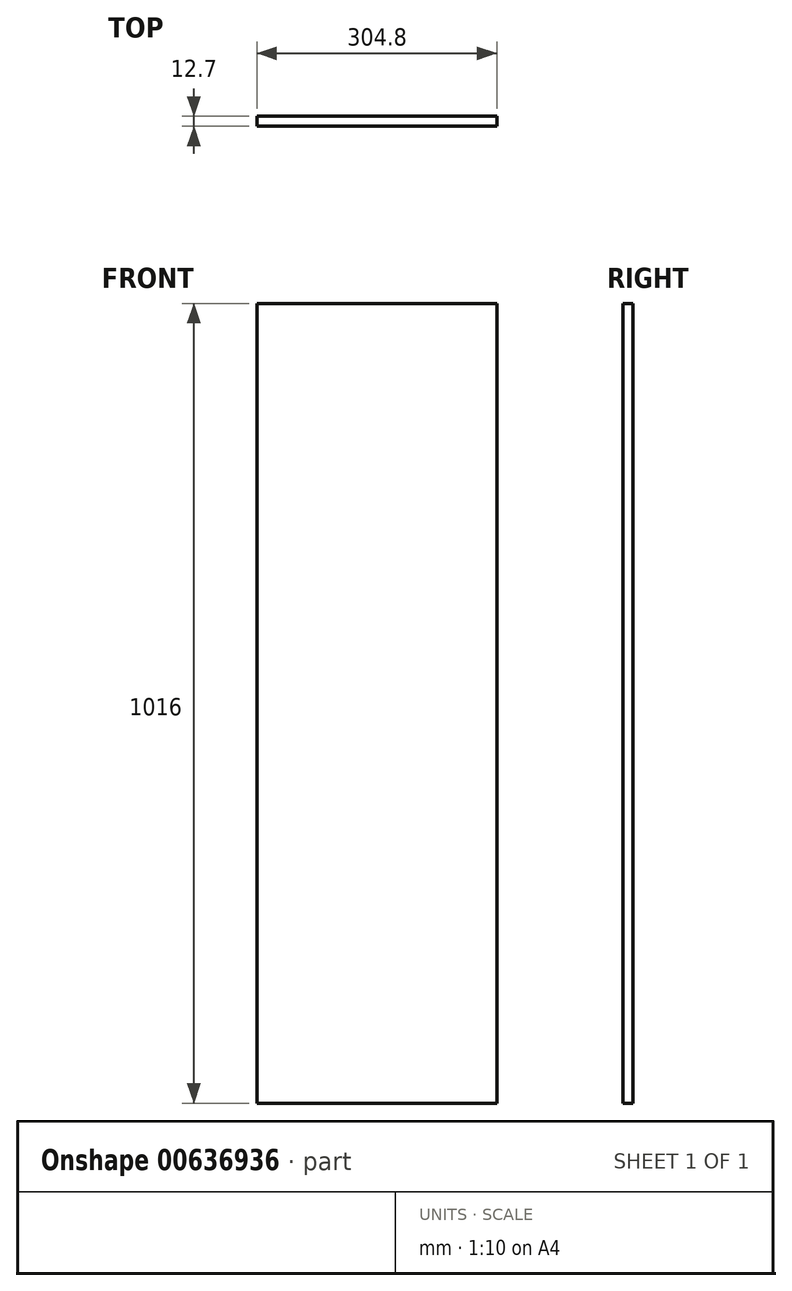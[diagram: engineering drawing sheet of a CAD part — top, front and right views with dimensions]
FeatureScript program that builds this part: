
annotation { "Feature Type Name" : "Feature", "Feature Type Description" : "" }
export const myFeature = defineFeature(function(context is Context, id is Id, definition is map)
    precondition{}
    {
        {
            var Q0;
            Q0=qCreatedBy(makeId("Front.planeOp"),FACE);
            var sketch = newSketch(context, id + "F0", { "sketchPlane" : qUnion([Q0])});
            skLineSegment(sketch, "E0.bottom", {"start": v(0, 0) * mm, "end": v(304.8, 0) * mm});
            skLineSegment(sketch, "E0.top", {"start": v(0, 1016) * mm, "end": v(304.8, 1016) * mm});
            skLineSegment(sketch, "E0.left", {"start": v(0, 0) * mm, "end": v(0, 1016) * mm});
            skLineSegment(sketch, "E0.right", {"start": v(304.8, 0) * mm, "end": v(304.8, 1016) * mm});
            skSolve(sketch);
        }
        {
            var Q0;
            Q0=makeQuery(id+"F0.imprint","IMPRINT",FACE,{"disambiguationData":[TD([[makeQuery(id+"F0.imprint","IMPRINT",EDGE,{"derivedFrom":sQuery(id+"F0.wireOp",EDGE,"E0.bottom")}),1.0]])]});
            extrude(context, id + "F1", {"entities" : qUnion([Q0]), "depth" : 12.7 * mm, "offsetDistance" : 25.4 * mm});
        }
    });
